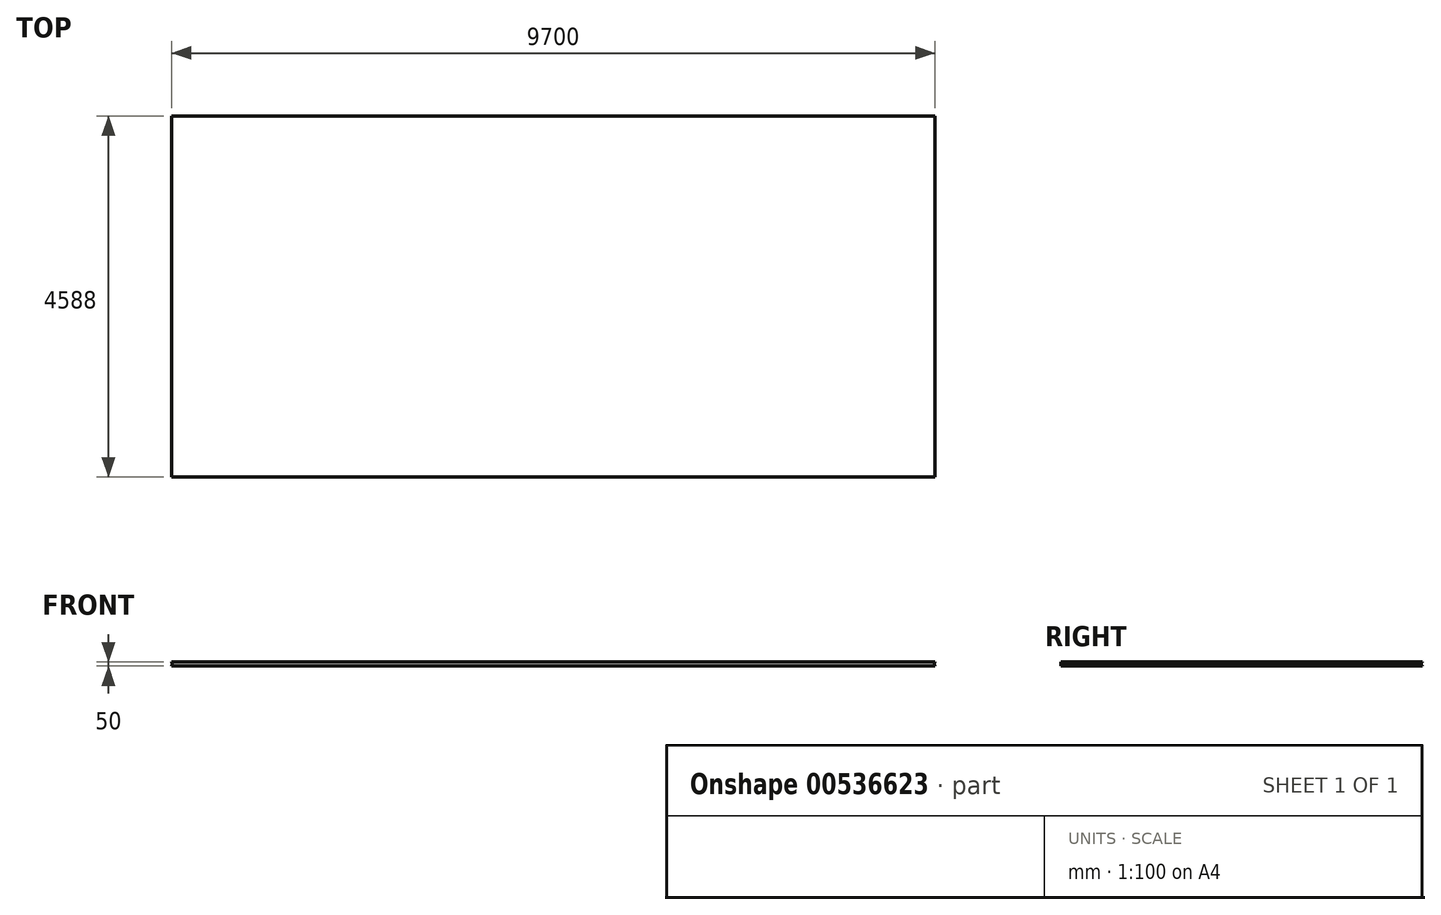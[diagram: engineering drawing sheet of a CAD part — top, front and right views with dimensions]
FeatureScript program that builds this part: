
annotation { "Feature Type Name" : "Feature", "Feature Type Description" : "" }
export const myFeature = defineFeature(function(context is Context, id is Id, definition is map)
    precondition{}
    {
        {
            var Q0;
            Q0=qCreatedBy(makeId("Top.planeOp"),FACE);
            var sketch = newSketch(context, id + "F0", { "sketchPlane" : qUnion([Q0])});
            skLineSegment(sketch, "E0.bottom", {"start": v(4850, -2294) * mm, "end": v(-4850, -2294) * mm});
            skLineSegment(sketch, "E0.top", {"start": v(4850, 2294) * mm, "end": v(-4850, 2294) * mm});
            skLineSegment(sketch, "E0.left", {"start": v(4850, -2294) * mm, "end": v(4850, 2294) * mm});
            skLineSegment(sketch, "E0.right", {"start": v(-4850, -2294) * mm, "end": v(-4850, 2294) * mm});
            skPoint(sketch, "E0.middle", {"position": v(0, 0) * mm});
            skSolve(sketch);
        }
        {
            var Q0;
            Q0=qSketchRegion(id+"F0",true);
            extrude(context, id + "F1", {"entities" : qUnion([Q0]), "depth" : 50 * mm});
        }
        {
            var Q0;
            Q0=makeQuery(id+"F1.opExtrude","CAP_FACE",FACE,{"disambiguationData":[OSD([sQuery(id+"F0.wireOp",EDGE,"E0.bottom"),sQuery(id+"F0.wireOp",EDGE,"E0.top"),sQuery(id+"F0.wireOp",EDGE,"E0.left"),sQuery(id+"F0.wireOp",EDGE,"E0.right")])],"isStart":false});
            var sketch = newSketch(context, id + "F2", { "sketchPlane" : qUnion([Q0])});
            skLineSegment(sketch, "E1.0", {"start": v(-4850, -2294) * mm, "end": v(-4850, 2294) * mm});
            skLineSegment(sketch, "E2.0", {"start": v(4850, 2294) * mm, "end": v(-4850, 2294) * mm});
            skLineSegment(sketch, "E3.0", {"start": v(4850, -2294) * mm, "end": v(4850, 2294) * mm});
            skSolve(sketch);
        }
        {
            var Q0;
            Q0=makeQuery(id+"F1.opExtrude","SWEPT_FACE",FACE,{"disambiguationData":[OSD([sQuery(id+"F0.wireOp",EDGE,"E0.bottom")])]});
            var sketch = newSketch(context, id + "F3", { "sketchPlane" : qUnion([Q0])});
            skLineSegment(sketch, "E4.bottom", {"start": v(-4850, 43.5) * mm, "end": v(-4840, 43.5) * mm});
            skLineSegment(sketch, "E4.top", {"start": v(-4850, 6.5) * mm, "end": v(-4840, 6.5) * mm});
            skLineSegment(sketch, "E4.left", {"start": v(-4850, 43.5) * mm, "end": v(-4850, 6.5) * mm});
            skLineSegment(sketch, "E4.right", {"start": v(-4840, 43.5) * mm, "end": v(-4840, 6.5) * mm});
            skSolve(sketch);
        }
        {
            var Q0;
            Q0=makeQuery(id+"F3.imprint","IMPRINT",FACE,{"disambiguationData":[TD([[makeQuery(id+"F3.imprint","IMPRINT",EDGE,{"derivedFrom":sQuery(id+"F3.wireOp",EDGE,"E4.bottom")}),-1.0]])]});
            var Q1;
            Q1=sQuery(id+"F2.wireOp",EDGE,"E1.0");
            var Q2;
            Q2=sQuery(id+"F2.wireOp",EDGE,"E2.0");
            var Q3;
            Q3=sQuery(id+"F2.wireOp",EDGE,"E3.0");
            sweep(context, id + "F4", {"operationType" : NewBodyOperationType.REMOVE, "profiles" : qUnion([Q0]), "path" : qUnion([Q1, Q2, Q3])});
        }
    });
